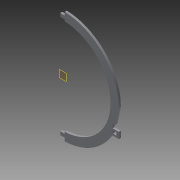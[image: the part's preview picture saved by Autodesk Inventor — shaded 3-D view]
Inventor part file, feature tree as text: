
AUTODESK INVENTOR PART (.ipt)
format: ipt  version: 2013 (Build 170138000, 138)  size: 123,392 bytes
history: native  units: in
note: dims shown in document units (in); Inventor stores cm internally (conversion verified against a paired STEP export)
features: sketch x2, extrude x2, plane x1
ambient origin geometry x8: Origin, YZ Plane, XZ Plane, XY Plane, X Axis, Y Axis, Z Axis, Center Point
feature tree (5):
  sketch  "Sketch1"  dims[d0=11.8in d1=13.3in d2=0.25in d3=0.25in d17=13.5in d19=13.5in]
  plane  "Work Plane1"
  sketch  "Sketch2"  dims[d20=11.5in d21=0.25in d22=0.25in d23=0.2in d24=0.55in d25=0.4in d26=0.2in d27=0.55in d28=0.4in d29=3.25in d32=0.217in d33=0.3in d34=0.4in d35=0.375in d38=2.5in d39=0.75in d40=0.5in d44=0.7015in d45=6.75in d46=6.75in d47=0.25in d48=0.0in d49=0.25in d50=0.0in]
  extrude  "Extrusion5"  Depth=13.5in
  extrude  "Extrusion6"  Depth=0.25in
